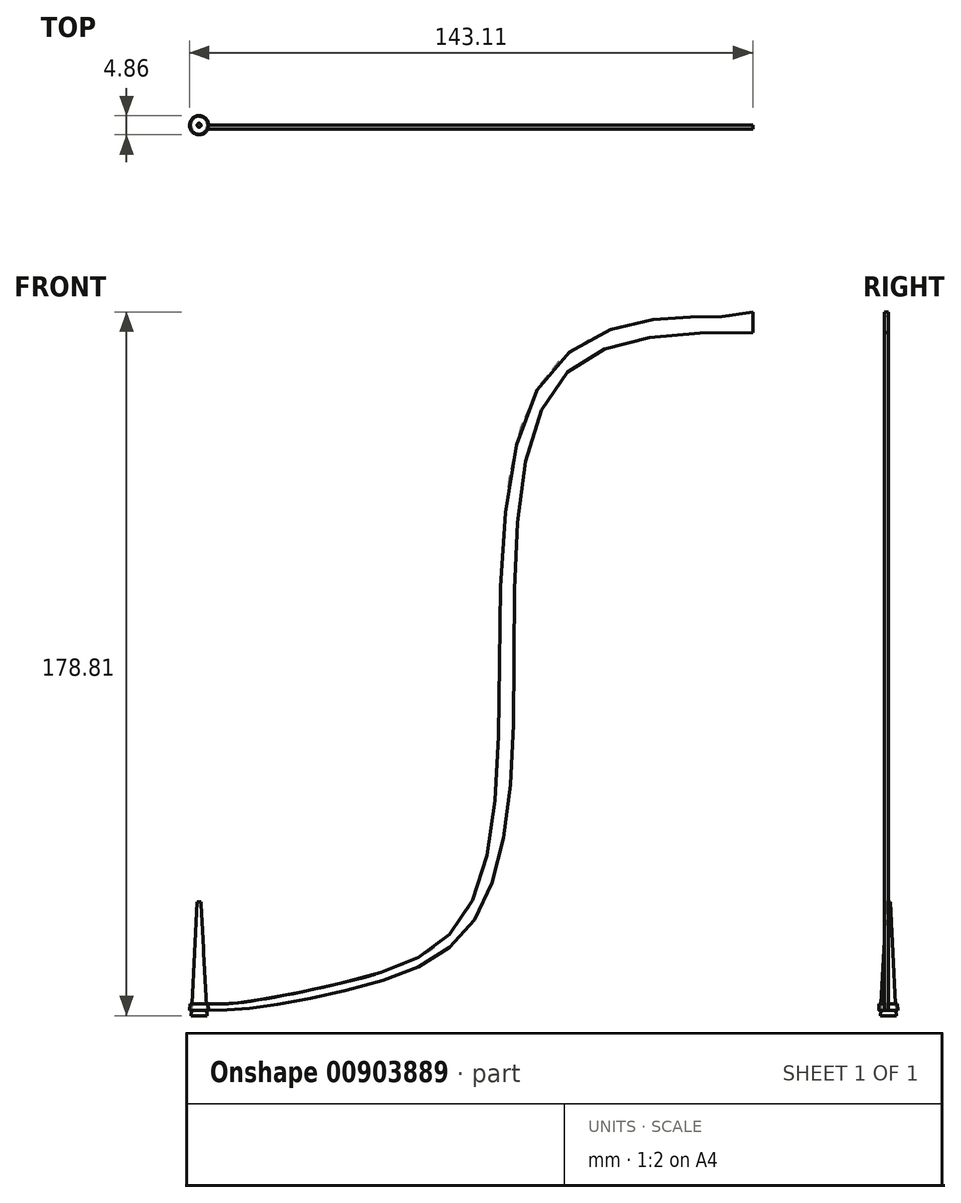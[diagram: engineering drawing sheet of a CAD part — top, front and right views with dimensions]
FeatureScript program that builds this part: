
annotation { "Feature Type Name" : "Feature", "Feature Type Description" : "" }
export const myFeature = defineFeature(function(context is Context, id is Id, definition is map)
    precondition{}
    {
        {
            var Q0;
            Q0=qCreatedBy(makeId("Top.planeOp"),FACE);
            var sketch = newSketch(context, id + "F0", { "sketchPlane" : qUnion([Q0])});
            skCircle(sketch, "E0", {"center": v(0, 0) * mm, "radius": 2 * mm});
            skSolve(sketch);
        }
        {
            var Q0;
            Q0=makeQuery(id+"F0.imprint","IMPRINT",FACE,{"disambiguationData":[TD([[makeQuery(id+"F0.imprint","IMPRINT",EDGE,{"derivedFrom":sQuery(id+"F0.wireOp",EDGE,"E0")}),1.0]])]});
            var Q1;
            Q1=sQuery(id+"F0.wireOp",EDGE,"E0");
            extrude(context, id + "F1", {"entities" : qUnion([Q0]), "surfaceEntities" : qUnion([Q1]), "depth" : 28.9 * mm, "offsetDistance" : 25 * mm, "hasDraft" : true, "draftAngle" : 3 * degree, "draftPullDirection" : true});
        }
        {
            var Q0;
            Q0=makeQuery(id+"F1.opExtrude","CAP_FACE",FACE,{"disambiguationData":[OSD([sQuery(id+"F0.wireOp",EDGE,"E0")])],"isStart":true});
            var sketch = newSketch(context, id + "F2", { "sketchPlane" : qUnion([Q0])});
            skCircle(sketch, "E1", {"center": v(0, 0) * mm, "radius": 2.5 * mm});
            skSolve(sketch);
        }
        {
            var Q0;
            Q0 = qSketchRegion(id + "F2", true);
            extrude(context, id + "F3", {"entities" : qUnion([Q0]), "oppositeDirection" : true, "depth" : 3 * mm, "offsetDistance" : 25 * mm, "hasDraft" : true, "draftAngle" : 3 * degree, "draftPullDirection" : true, "hasSecondDirection" : true, "secondDirectionOppositeDirection" : true, "secondDirectionDepth" : 1.4 * mm});
        }
        {
            var Q0;
            Q0=qCreatedBy(makeId("Front.planeOp"),FACE);
            var sketch = newSketch(context, id + "F4", { "sketchPlane" : qUnion([Q0])});
            skFitSpline(sketch, "E2", {"points": [v(2.39, 1.38) * mm, v(12.25, 1.78) * mm, v(37.08, 6.38) * mm, v(66.67, 20.12) * mm, v(79.8, 72.61) * mm, v(90.92, 160.45) * mm, v(140.68, 173.57) * mm], "startDerivative": vector(106.31, -0.13) * mm, "endDerivative": vector(312.74, -0.3) * mm});
            skFitSpline(sketch, "E3", {"points": [v(2.32, 2.97) * mm, v(5.26, 2.97) * mm, v(11.48, 3.44) * mm, v(36.54, 8.39) * mm, v(64.36, 21.38) * mm, v(76.07, 71.66) * mm, v(87.57, 161.8) * mm, v(120.9, 177.43) * mm, v(140.68, 178.8) * mm], "startDerivative": vector(70.1, -0.67) * mm, "endDerivative": vector(188.9, 52.11) * mm});
            skLineSegment(sketch, "E4", {"start": v(2.39, 1.38) * mm, "end": v(2.32, 2.97) * mm});
            skLineSegment(sketch, "E5", {"start": v(140.68, 173.57) * mm, "end": v(140.68, 178.8) * mm});
            skSolve(sketch);
        }
        {
            var Q0;
            Q0 = qSketchRegion(id + "F4", true);
            extrude(context, id + "F5", {"entities" : qUnion([Q0]), "operationType" : NewBodyOperationType.ADD, "depth" : 1 * mm, "offsetDistance" : 25 * mm});
        }
    });
